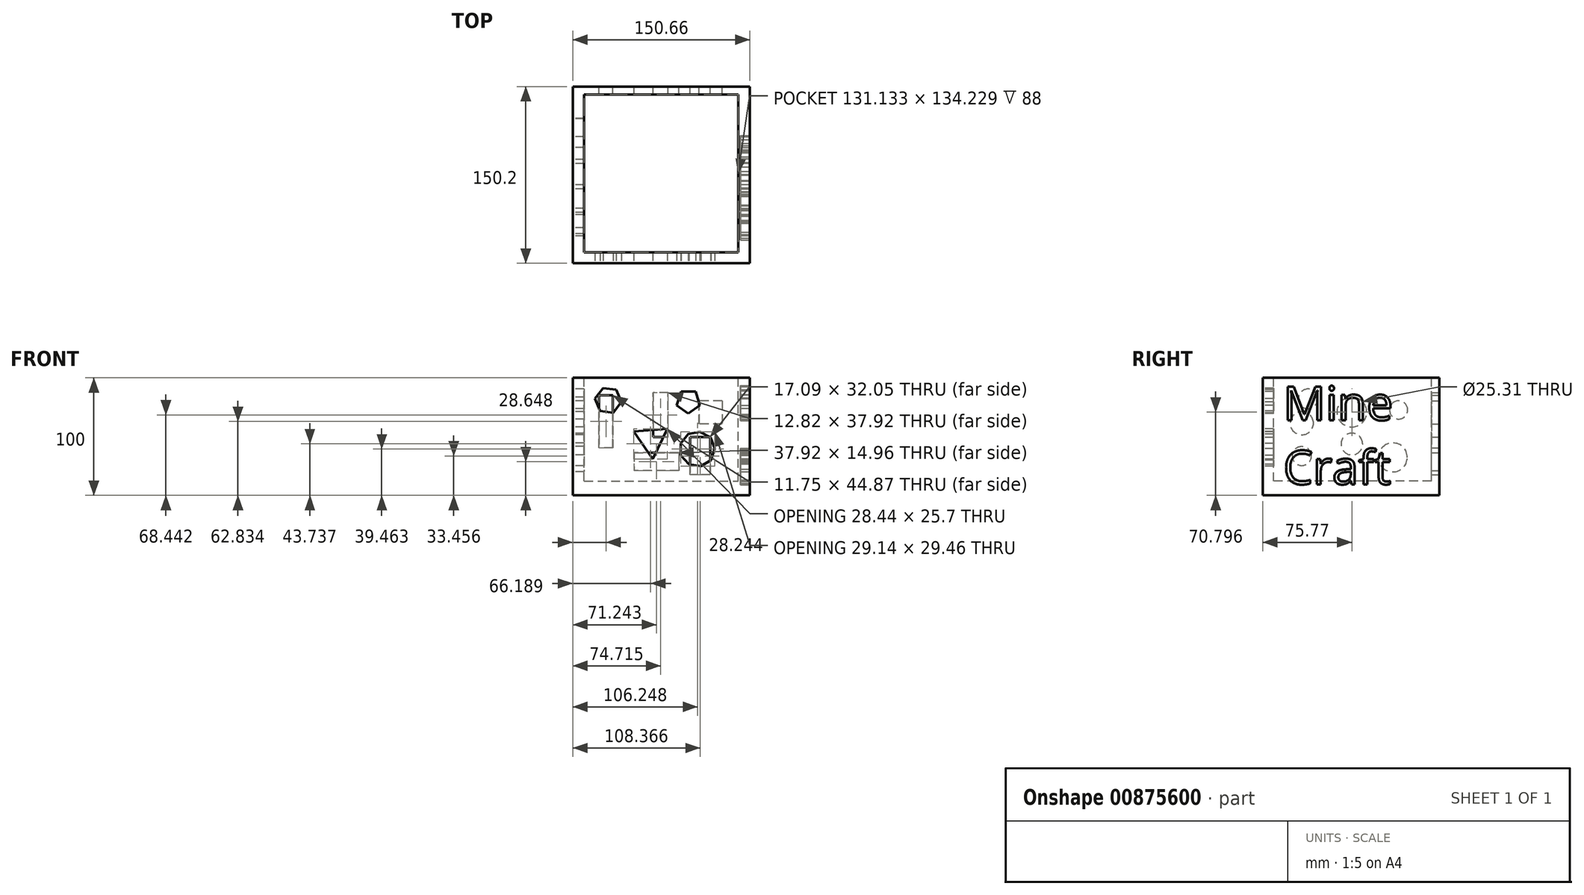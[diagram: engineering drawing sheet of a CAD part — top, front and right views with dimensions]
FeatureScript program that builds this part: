
annotation { "Feature Type Name" : "Feature", "Feature Type Description" : "" }
export const myFeature = defineFeature(function(context is Context, id is Id, definition is map)
    precondition{}
    {
        {
            var Q0;
            Q0=qCreatedBy(makeId("Top.planeOp"),FACE);
            var sketch = newSketch(context, id + "F0", { "sketchPlane" : qUnion([Q0])});
            skLineSegment(sketch, "E0.bottom", {"start": v(-74.22, 74.43) * mm, "end": v(76.44, 74.43) * mm});
            skLineSegment(sketch, "E0.top", {"start": v(-74.22, -75.77) * mm, "end": v(76.44, -75.77) * mm});
            skLineSegment(sketch, "E0.left", {"start": v(-74.22, 74.43) * mm, "end": v(-74.22, -75.77) * mm});
            skLineSegment(sketch, "E0.right", {"start": v(76.44, 74.43) * mm, "end": v(76.44, -75.77) * mm});
            skSolve(sketch);
        }
        {
            var Q0;
            Q0=makeQuery(id+"F0.imprint","IMPRINT",FACE,{"disambiguationData":[TD([[makeQuery(id+"F0.imprint","IMPRINT",EDGE,{"derivedFrom":sQuery(id+"F0.wireOp",EDGE,"E0.bottom")}),-1.0]])]});
            extrude(context, id + "F1", {"entities" : qUnion([Q0]), "depth" : 100 * mm, "offsetDistance" : 25 * mm});
        }
        {
            var Q0;
            Q0=makeQuery(id+"F1.opExtrude","SWEPT_FACE",FACE,{"disambiguationData":[OSD([sQuery(id+"F0.wireOp",EDGE,"E0.right")])]});
            var sketch = newSketch(context, id + "F2", { "sketchPlane" : qUnion([Q0])});
            skSolve(sketch);
        }
        {
            var Q0;
            Q0=makeQuery(id+"F1.opExtrude","CAP_FACE",FACE,{"disambiguationData":[OSD([sQuery(id+"F0.wireOp",EDGE,"E0.bottom"),sQuery(id+"F0.wireOp",EDGE,"E0.top"),sQuery(id+"F0.wireOp",EDGE,"E0.left"),sQuery(id+"F0.wireOp",EDGE,"E0.right")])],"isStart":false});
            var sketch = newSketch(context, id + "F3", { "sketchPlane" : qUnion([Q0])});
            skLineSegment(sketch, "E1.bottom", {"start": v(-64.52, 67.74) * mm, "end": v(66.62, 67.74) * mm});
            skLineSegment(sketch, "E1.top", {"start": v(-64.52, -66.49) * mm, "end": v(66.62, -66.49) * mm});
            skLineSegment(sketch, "E1.left", {"start": v(-64.52, 67.74) * mm, "end": v(-64.52, -66.49) * mm});
            skLineSegment(sketch, "E1.right", {"start": v(66.62, 67.74) * mm, "end": v(66.62, -66.49) * mm});
            skSolve(sketch);
        }
        {
            var Q0;
            Q0=makeQuery(id+"F3.imprint","IMPRINT",FACE,{"disambiguationData":[TD([[makeQuery(id+"F3.imprint","IMPRINT",EDGE,{"derivedFrom":sQuery(id+"F3.wireOp",EDGE,"E1.bottom")}),-1.0]])]});
            extrude(context, id + "F4", {"entities" : qUnion([Q0]), "operationType" : NewBodyOperationType.REMOVE, "oppositeDirection" : true, "depth" : 88 * mm, "offsetDistance" : 25 * mm});
        }
        {
            var Q0;
            Q0=makeQuery(id+"F1.opExtrude","SWEPT_FACE",FACE,{"disambiguationData":[OSD([sQuery(id+"F0.wireOp",EDGE,"E0.top")])]});
            var sketch = newSketch(context, id + "F5", { "sketchPlane" : qUnion([Q0])});
            skCircle(sketch, "E2.cCircle", {"center": v(-44.15, 80.77) * mm, "radius": 9.83 * mm, "construction": true});
            skLineSegment(sketch, "E2.0", {"start": v(-55.4, 82.2) * mm, "end": v(-48.53, 91.24) * mm});
            skLineSegment(sketch, "E2.1", {"start": v(-48.53, 91.24) * mm, "end": v(-37.27, 89.8) * mm});
            skLineSegment(sketch, "E2.2", {"start": v(-37.27, 89.8) * mm, "end": v(-32.9, 79.33) * mm});
            skLineSegment(sketch, "E2.3", {"start": v(-32.9, 79.33) * mm, "end": v(-39.76, 70.3) * mm});
            skLineSegment(sketch, "E2.4", {"start": v(-39.76, 70.3) * mm, "end": v(-51.02, 71.74) * mm});
            skLineSegment(sketch, "E2.5", {"start": v(-51.02, 71.74) * mm, "end": v(-55.4, 82.2) * mm});
            skPoint(sketch, "E2.0.midPoint", {"position": v(-51.97, 86.72) * mm});
            skCircle(sketch, "E3.cCircle", {"center": v(-7.42, 47.31) * mm, "radius": 8.23 * mm, "construction": true});
            skLineSegment(sketch, "E3.0", {"start": v(6.2, 56.58) * mm, "end": v(-6.2, 30.89) * mm});
            skLineSegment(sketch, "E3.1", {"start": v(-6.2, 30.89) * mm, "end": v(-22.25, 54.46) * mm});
            skLineSegment(sketch, "E3.2", {"start": v(-22.25, 54.46) * mm, "end": v(6.2, 56.58) * mm});
            skPoint(sketch, "E3.0.midPoint", {"position": v(0, 43.74) * mm});
            skCircle(sketch, "E4.cCircle", {"center": v(24.05, 79.84) * mm, "radius": 8.41 * mm, "construction": true});
            skLineSegment(sketch, "E4.0", {"start": v(17.93, 88.26) * mm, "end": v(30.16, 88.26) * mm});
            skLineSegment(sketch, "E4.1", {"start": v(30.16, 88.26) * mm, "end": v(33.94, 76.63) * mm});
            skLineSegment(sketch, "E4.2", {"start": v(33.94, 76.63) * mm, "end": v(24.05, 69.44) * mm});
            skLineSegment(sketch, "E4.3", {"start": v(24.05, 69.44) * mm, "end": v(14.16, 76.63) * mm});
            skLineSegment(sketch, "E4.4", {"start": v(14.16, 76.63) * mm, "end": v(17.93, 88.26) * mm});
            skPoint(sketch, "E4.0.midPoint", {"position": v(24.05, 88.26) * mm});
            skCircle(sketch, "E5.cCircle", {"center": v(31.64, 39.4) * mm, "radius": 14.06 * mm, "construction": true});
            skLineSegment(sketch, "E5.0", {"start": v(33.87, 54.2) * mm, "end": v(42.86, 49.3) * mm});
            skLineSegment(sketch, "E5.1", {"start": v(42.86, 49.3) * mm, "end": v(46.6, 39.77) * mm});
            skLineSegment(sketch, "E5.2", {"start": v(46.6, 39.77) * mm, "end": v(43.34, 30.07) * mm});
            skLineSegment(sketch, "E5.3", {"start": v(43.34, 30.07) * mm, "end": v(34.6, 24.73) * mm});
            skLineSegment(sketch, "E5.4", {"start": v(34.6, 24.73) * mm, "end": v(24.48, 26.26) * mm});
            skLineSegment(sketch, "E5.5", {"start": v(24.48, 26.26) * mm, "end": v(17.71, 33.94) * mm});
            skLineSegment(sketch, "E5.6", {"start": v(17.71, 33.94) * mm, "end": v(17.46, 44.17) * mm});
            skLineSegment(sketch, "E5.7", {"start": v(17.46, 44.17) * mm, "end": v(23.84, 52.17) * mm});
            skLineSegment(sketch, "E5.8", {"start": v(23.84, 52.17) * mm, "end": v(33.87, 54.2) * mm});
            skPoint(sketch, "E5.0.midPoint", {"position": v(38.37, 51.74) * mm});
            skPoint(sketch, "E6.0.midPoint", {"position": v(-19.85, 23.43) * mm});
            skText(sketch, "E7", { "text": "B", "fontName": "OpenSans-Regular.ttf"});
            const initialGuessF5  = {"E7": [-0.05517, 0.02455, 1, 0, 0.02991]};
            skSetInitialGuess(sketch, initialGuessF5);
            skSolve(sketch);
        }
        {
            var Q0;
            Q0=makeQuery(id+"F5.imprint","IMPRINT",FACE,{"disambiguationData":[TD([[makeQuery(id+"F5.imprint","IMPRINT",EDGE,{"derivedFrom":sQuery(id+"F5.wireOp",EDGE,"E4.0")}),-1.0]])]});
            var Q1;
            Q1=makeQuery(id+"F5.imprint","IMPRINT",FACE,{"disambiguationData":[TD([[makeQuery(id+"F5.imprint","IMPRINT",EDGE,{"derivedFrom":sQuery(id+"F5.wireOp",EDGE,"E5.0")}),-1.0]])]});
            var Q2;
            Q2=makeQuery(id+"F5.imprint","IMPRINT",FACE,{"disambiguationData":[TD([[makeQuery(id+"F5.imprint","IMPRINT",EDGE,{"derivedFrom":sQuery(id+"F5.wireOp",EDGE,"E2.0")}),-1.0]])]});
            var Q3;
            Q3=makeQuery(id+"F5.imprint","IMPRINT",FACE,{"disambiguationData":[TD([[makeQuery(id+"F5.imprint","IMPRINT",EDGE,{"derivedFrom":sQuery(id+"F5.wireOp",EDGE,"E3.0")}),-1.0]])]});
            extrude(context, id + "F6", {"entities" : qUnion([Q0, Q1, Q2, Q3]), "operationType" : NewBodyOperationType.REMOVE, "oppositeDirection" : true, "depth" : 25 * mm, "offsetDistance" : 25 * mm});
        }
        {
            var Q0;
            Q0=makeQuery(id+"F1.opExtrude","SWEPT_FACE",FACE,{"disambiguationData":[OSD([sQuery(id+"F0.wireOp",EDGE,"E0.left")])]});
            var sketch = newSketch(context, id + "F7", { "sketchPlane" : qUnion([Q0])});
            skCircle(sketch, "E8", {"center": v(0, 70.8) * mm, "radius": 12.66 * mm});
            skCircle(sketch, "E9", {"center": v(-34.89, 32.27) * mm, "radius": 12.33 * mm});
            skCircle(sketch, "E10", {"center": v(42.54, 33.4) * mm, "radius": 8.1 * mm});
            skCircle(sketch, "E11", {"center": v(42.54, 61.35) * mm, "radius": 9.89 * mm});
            skCircle(sketch, "E12", {"center": v(0, 43.6) * mm, "radius": 9.2 * mm});
            skCircle(sketch, "E13", {"center": v(-39.8, 72.68) * mm, "radius": 7.75 * mm});
            skCircle(sketch, "E14", {"center": v(37.25, 82.13) * mm, "radius": 8.32 * mm});
            skSolve(sketch);
        }
        {
            var Q0;
            Q0 = qSketchRegion(id + "F7", true);
            var Q1;
            Q1=makeQuery(id+"F7.imprint","IMPRINT",FACE,{"disambiguationData":[TD([[makeQuery(id+"F7.imprint","IMPRINT",EDGE,{"derivedFrom":sQuery(id+"F7.wireOp",EDGE,"E8")}),1.0]])]});
            extrude(context, id + "F8", {"entities" : qUnion([Q0, Q1]), "operationType" : NewBodyOperationType.REMOVE, "oppositeDirection" : true, "depth" : 25 * mm, "offsetDistance" : 25 * mm});
        }
        {
            var Q0;
            Q0=makeQuery(id+"F1.opExtrude","SWEPT_FACE",FACE,{"disambiguationData":[OSD([sQuery(id+"F0.wireOp",EDGE,"E0.bottom")])]});
            var sketch = newSketch(context, id + "F9", { "sketchPlane" : qUnion([Q0])});
            skLineSegment(sketch, "E15.bottom", {"start": v(-52.84, 80.46) * mm, "end": v(-33.08, 80.46) * mm});
            skLineSegment(sketch, "E15.top", {"start": v(-52.84, 60.7) * mm, "end": v(-33.08, 60.7) * mm});
            skLineSegment(sketch, "E15.left", {"start": v(-52.84, 80.46) * mm, "end": v(-52.84, 60.7) * mm});
            skLineSegment(sketch, "E15.right", {"start": v(-33.08, 80.46) * mm, "end": v(-33.08, 60.7) * mm});
            skLineSegment(sketch, "E16.bottom", {"start": v(40.1, 40.4) * mm, "end": v(51.85, 40.4) * mm});
            skLineSegment(sketch, "E16.top", {"start": v(40.1, 85.27) * mm, "end": v(51.85, 85.27) * mm});
            skLineSegment(sketch, "E16.left", {"start": v(40.1, 40.4) * mm, "end": v(40.1, 85.27) * mm});
            skLineSegment(sketch, "E16.right", {"start": v(51.85, 40.4) * mm, "end": v(51.85, 85.27) * mm});
            skLineSegment(sketch, "E17.bottom", {"start": v(-15.99, 36.13) * mm, "end": v(21.94, 36.13) * mm});
            skLineSegment(sketch, "E17.top", {"start": v(-15.99, 21.17) * mm, "end": v(21.94, 21.17) * mm});
            skLineSegment(sketch, "E17.left", {"start": v(-15.99, 36.13) * mm, "end": v(-15.99, 21.17) * mm});
            skLineSegment(sketch, "E17.right", {"start": v(21.94, 36.13) * mm, "end": v(21.94, 21.17) * mm});
            skLineSegment(sketch, "E18.bottom", {"start": v(-6.9, 49.48) * mm, "end": v(5.91, 49.48) * mm});
            skLineSegment(sketch, "E18.top", {"start": v(-6.9, 87.4) * mm, "end": v(5.91, 87.4) * mm});
            skLineSegment(sketch, "E18.left", {"start": v(-6.9, 49.48) * mm, "end": v(-6.9, 87.4) * mm});
            skLineSegment(sketch, "E18.right", {"start": v(5.91, 49.48) * mm, "end": v(5.91, 87.4) * mm});
            skLineSegment(sketch, "E19.bottom", {"start": v(-42.7, 49.48) * mm, "end": v(-25.6, 49.48) * mm});
            skLineSegment(sketch, "E19.top", {"start": v(-42.7, 17.43) * mm, "end": v(-25.6, 17.43) * mm});
            skLineSegment(sketch, "E19.left", {"start": v(-42.7, 49.48) * mm, "end": v(-42.7, 17.43) * mm});
            skLineSegment(sketch, "E19.right", {"start": v(-25.6, 49.48) * mm, "end": v(-25.6, 17.43) * mm});
            skSolve(sketch);
        }
        {
            var Q0;
            Q0=makeQuery(id+"F9.imprint","IMPRINT",FACE,{"disambiguationData":[TD([[makeQuery(id+"F9.imprint","IMPRINT",EDGE,{"derivedFrom":sQuery(id+"F9.wireOp",EDGE,"E16.bottom")}),1.0]])]});
            var Q1;
            Q1=makeQuery(id+"F9.imprint","IMPRINT",FACE,{"disambiguationData":[TD([[makeQuery(id+"F9.imprint","IMPRINT",EDGE,{"derivedFrom":sQuery(id+"F9.wireOp",EDGE,"E17.bottom")}),-1.0]])]});
            var Q2;
            Q2=makeQuery(id+"F9.imprint","IMPRINT",FACE,{"disambiguationData":[TD([[makeQuery(id+"F9.imprint","IMPRINT",EDGE,{"derivedFrom":sQuery(id+"F9.wireOp",EDGE,"E18.bottom")}),1.0]])]});
            var Q3;
            Q3=makeQuery(id+"F9.imprint","IMPRINT",FACE,{"disambiguationData":[TD([[makeQuery(id+"F9.imprint","IMPRINT",EDGE,{"derivedFrom":sQuery(id+"F9.wireOp",EDGE,"E19.bottom")}),-1.0]])]});
            var Q4;
            Q4=makeQuery(id+"F9.imprint","IMPRINT",FACE,{"disambiguationData":[TD([[makeQuery(id+"F9.imprint","IMPRINT",EDGE,{"derivedFrom":sQuery(id+"F9.wireOp",EDGE,"E15.bottom")}),-1.0]])]});
            extrude(context, id + "F10", {"entities" : qUnion([Q0, Q1, Q2, Q3, Q4]), "operationType" : NewBodyOperationType.REMOVE, "oppositeDirection" : true, "depth" : 25 * mm, "offsetDistance" : 25 * mm});
        }
        {
            var Q0;
            {var subQ0=sQuery(id+"F0.wireOp",EDGE,"E0.right");Q0=makeQuery(id+"F2.imprint","IMPRINT",FACE,{"disambiguationData":[TD([[makeQuery(id+"F2.imprint","IMPRINT",EDGE,{"derivedFrom":makeQuery(id+"F1.opExtrude","CAP_EDGE",EDGE,{"disambiguationData":[OSD([subQ0])],"isStart":true})}),-1.0]])]});}
            var sketch = newSketch(context, id + "F11", { "sketchPlane" : qUnion([Q0])});
            skText(sketch, "E20", { "text": "Mine\nCraft", "fontName": "OpenSans-Regular.ttf"});
            const initialGuessF11  = {"E20": [-0.05834, 0.0639, 1, 0, 0.02884]};
            skSetInitialGuess(sketch, initialGuessF11);
            skSolve(sketch);
        }
        {
            var Q0;
            Q0 = qSketchRegion(id + "F11", true);
            extrude(context, id + "F12", {"entities" : qUnion([Q0]), "operationType" : NewBodyOperationType.REMOVE, "oppositeDirection" : true, "depth" : 8 * mm, "offsetDistance" : 25 * mm});
        }
    });
